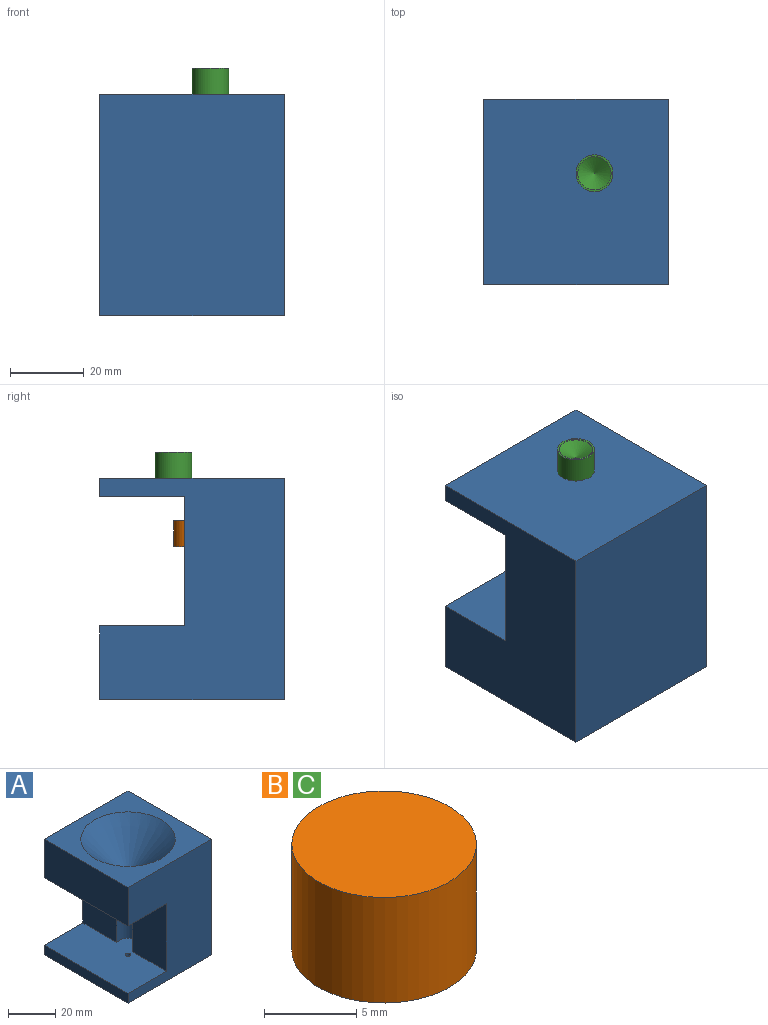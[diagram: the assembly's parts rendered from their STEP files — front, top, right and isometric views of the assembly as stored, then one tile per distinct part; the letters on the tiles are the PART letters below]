
ASSEMBLY  parts=3 mates=3
PART A: 18 faces, bbox 50x50x60 mm
  f0: plane 35x22.76mm, normal (-1,0,0), area 759.1mm2, adj f5,f10,f11,f12,f13,f14
  f1: plane 35x22.76mm, normal (-1,0,0), area 759.1mm2, adj f3,f10,f11,f12,f13,f14
  f2: plane 50x5mm, normal (-1,0,0), area 250mm2, adj f3,f5,f8,f11
  f3: plane 60x50mm, normal (0,1,0), area 2195mm2, adj f1,f2,f4,f6,f7,f8,f10,f11
  f4: plane 50x20mm, normal (-1,0,0), area 1000mm2, adj f3,f5,f7,f10
  f5: plane 60x50mm, normal (0,-1,0), area 2195mm2, adj f0,f2,f4,f6,f7,f8,f10,f11
  f6: plane 60x50mm, normal (1,0,0), area 3000mm2, adj f3,f5,f7,f8
  f7: plane 50x50mm, normal (0,0,1), area 1243.4mm2, adj f3,f4,f5,f6,f9
  f8: plane 50x50mm, normal (0,0,-1), area 2496.2mm2, adj f2,f3,f5,f6,f15
  f9: cone r=20mm half-angle=45deg, axis (0,0,1), area 1737.2mm2, adj f7,f12
  f10: plane 50x23mm, normal (0,0,-1), area 1143.1mm2, adj f0,f1,f3,f4,f5,f12,f16
  f11: plane 50x30.15mm, normal (0,0,1), area 1207.9mm2, adj f0,f1,f2,f3,f5,f13,f15
  f12: cylinder r=3mm len=23mm, axis (0,0,1), area 332.6mm2, adj f0,f1,f9,f10,f14
  f13: cylinder r=5.15mm len=15mm, axis (0,0,-1), area 304.3mm2, adj f0,f1,f11,f14
  f14: plane 10.3x7.15mm, normal (0,0,-1), area 36.6mm2, adj f0,f1,f12,f13
  f15: cylinder r=1.1mm len=5mm, axis (0,0,-1), area 34.6mm2, adj f8,f11
  f16: cylinder r=1.1mm len=5mm, axis (0,0,-1), area 34.6mm2, adj f10,f17
  f17: plane 2.2x2.2mm, normal (0,0,-1), area 3.8mm2, adj f16
PART B: 5 faces, bbox 10x10x7 mm
  f0: cylinder r=5mm len=10mm, axis (0,0,-1), area 219.9mm2, adj f1,f2
  f1: plane 10x10mm, normal (0,0,1), area 78.5mm2, adj f0
  f2: plane 10x10mm, normal (0,0,-1), area 14.9mm2, adj f0,f4
  f3: cone r=0mm half-angle=59deg, axis (0,0,-1), area 74.2mm2, adj f4
  f4: cylinder r=4.5mm len=9mm, axis (0,0,-1), area 2.8mm2, adj f2,f3
PART C: same geometry as B
PLACE A rot(axis=(0.71,-0.71,0),180deg) t=(-31.29,-25.33,24.05)mm
PLACE B rot(axis=(-0.31,-0.06,-0.95),0deg) t=(-31.29,-25.33,5.51)mm
PLACE C rot(axis=(1,0,0),180deg) t=(-26.29,-20.33,31.05)mm
MATE slider A.f13 <-> B.f0  axis (0,0,1) through (-31.29,-25.33,11.55)mm
MATE revolute C.f0 <-> A.f15  axis (0,0,-1) through (-26.29,-20.33,24.05)mm
MATE slider A.f12 <-> A.f13  axis (0,0,1) through (-31.29,-25.33,4.05)mm
